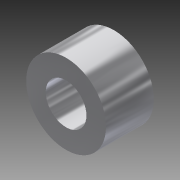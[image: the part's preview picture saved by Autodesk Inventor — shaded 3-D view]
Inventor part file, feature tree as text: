
AUTODESK INVENTOR PART (.ipt)
format: ipt  version: 2014 SP1 (Build 180222100, 222)  size: 86,016 bytes
history: native  units: in
note: dims shown in document units (in); Inventor stores cm internally (conversion verified against a paired STEP export)
features: extrude x1, sketch x1
ambient origin geometry x8: Origin, YZ Plane, XZ Plane, XY Plane, X Axis, Y Axis, Z Axis, Center Point
bodies: Solid1 (feature_tree)
feature tree (2):
  extrude  "Extrusion1"  Depth=0.3937in
  sketch  "Sketch1"  dims[d0=0.2008in d1=0.3937in d2=0.2362in d3=0.0in]
